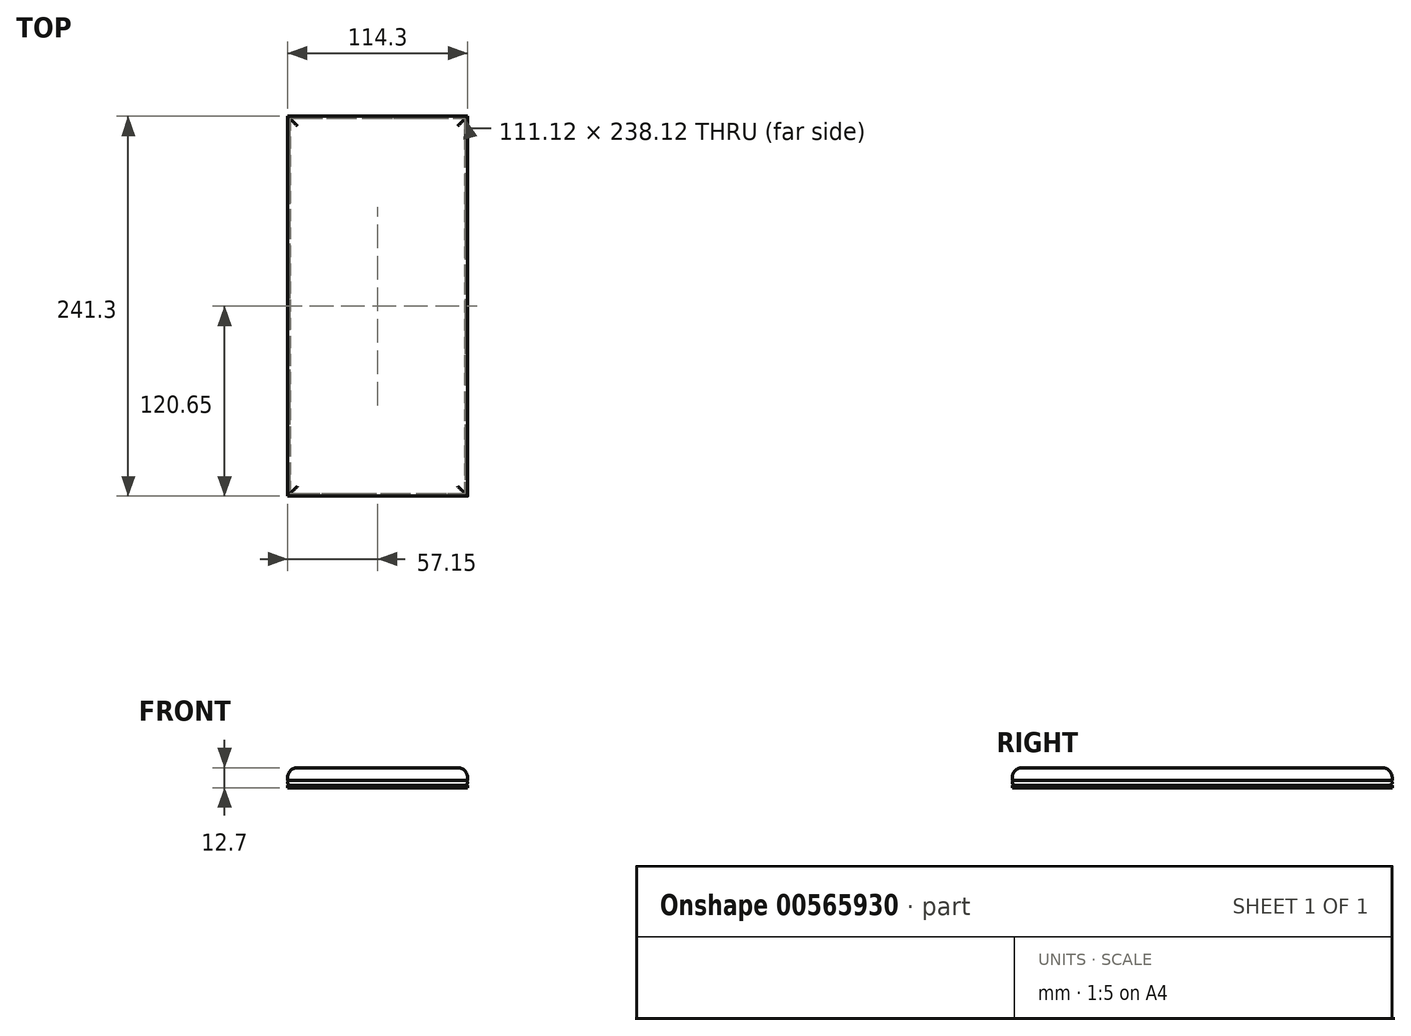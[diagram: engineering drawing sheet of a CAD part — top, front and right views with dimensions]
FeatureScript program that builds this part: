
annotation { "Feature Type Name" : "Feature", "Feature Type Description" : "" }
export const myFeature = defineFeature(function(context is Context, id is Id, definition is map)
    precondition{}
    {
        {
            var Q0;
            Q0=qCreatedBy(makeId("Top.planeOp"),FACE);
            var sketch = newSketch(context, id + "F0", { "sketchPlane" : qUnion([Q0])});
            skLineSegment(sketch, "E0.bottom", {"start": v(-57.15, 120.65) * mm, "end": v(57.15, 120.65) * mm});
            skLineSegment(sketch, "E0.top", {"start": v(-57.15, -120.65) * mm, "end": v(57.15, -120.65) * mm});
            skLineSegment(sketch, "E0.left", {"start": v(-57.15, 120.65) * mm, "end": v(-57.15, -120.65) * mm});
            skLineSegment(sketch, "E0.right", {"start": v(57.15, 120.65) * mm, "end": v(57.15, -120.65) * mm});
            skLineSegment(sketch, "E1", {"start": v(-57.15, 120.65) * mm, "end": v(57.15, -120.65) * mm, "construction": true});
            skSolve(sketch);
        }
        {
            var Q0;
            Q0 = qSketchRegion(id + "F0", true);
            extrude(context, id + "F1", {"entities" : qUnion([Q0]), "endBound" : BoundingType.SYMMETRIC, "depth" : 12.7 * mm, "offsetDistance" : 25.4 * mm});
        }
        {
            var Q0;
            Q0=makeQuery(id+"F1.opExtrude","CAP_FACE",FACE,{"disambiguationData":[OSD([sQuery(id+"F0.wireOp",EDGE,"E0.bottom"),sQuery(id+"F0.wireOp",EDGE,"E0.top"),sQuery(id+"F0.wireOp",EDGE,"E0.left"),sQuery(id+"F0.wireOp",EDGE,"E0.right")])],"isStart":false});
            fillet(context, id + "F2", {"entities" : qUnion([Q0]), "radius" : 6.35 * mm, "tangentPropagation" : true, "allowEdgeOverflow" : false});
        }
        {
            var Q0;
            Q0=makeQuery(id+"F1.opExtrude","SWEPT_FACE",FACE,{"disambiguationData":[OSD([sQuery(id+"F0.wireOp",EDGE,"E0.top")])]});
            var sketch = newSketch(context, id + "F3", { "sketchPlane" : qUnion([Q0])});
            skArc(sketch, "E2", {"start": v(55.56, -4.76) * mm, "mid": v(57.15, -3.18) * mm, "end": v(55.56, -1.59) * mm});
            skLineSegment(sketch, "E3", {"start": v(55.56, -1.59) * mm, "end": v(57.15, -1.59) * mm});
            skLineSegment(sketch, "E4", {"start": v(55.56, -4.76) * mm, "end": v(57.15, -4.76) * mm});
            skLineSegment(sketch, "E5", {"start": v(57.15, -1.59) * mm, "end": v(57.15, -4.76) * mm});
            skSolve(sketch);
        }
        {
            var Q0;
            Q0 = qSketchRegion(id + "F3", true);
            var Q1;
            Q1=makeQuery(id+"F1.opExtrude","CAP_EDGE",EDGE,{"disambiguationData":[OSD([sQuery(id+"F0.wireOp",EDGE,"E0.right")])],"isStart":true});
            var Q2;
            Q2=makeQuery(id+"F1.opExtrude","CAP_EDGE",EDGE,{"disambiguationData":[OSD([sQuery(id+"F0.wireOp",EDGE,"E0.top")])],"isStart":true});
            var Q3;
            Q3=makeQuery(id+"F1.opExtrude","CAP_EDGE",EDGE,{"disambiguationData":[OSD([sQuery(id+"F0.wireOp",EDGE,"E0.bottom")])],"isStart":true});
            var Q4;
            Q4=makeQuery(id+"F1.opExtrude","CAP_EDGE",EDGE,{"disambiguationData":[OSD([sQuery(id+"F0.wireOp",EDGE,"E0.left")])],"isStart":true});
            sweep(context, id + "F4", {"operationType" : NewBodyOperationType.REMOVE, "profiles" : qUnion([Q0]), "path" : qUnion([Q1, Q2, Q3, Q4])});
        }
    });
